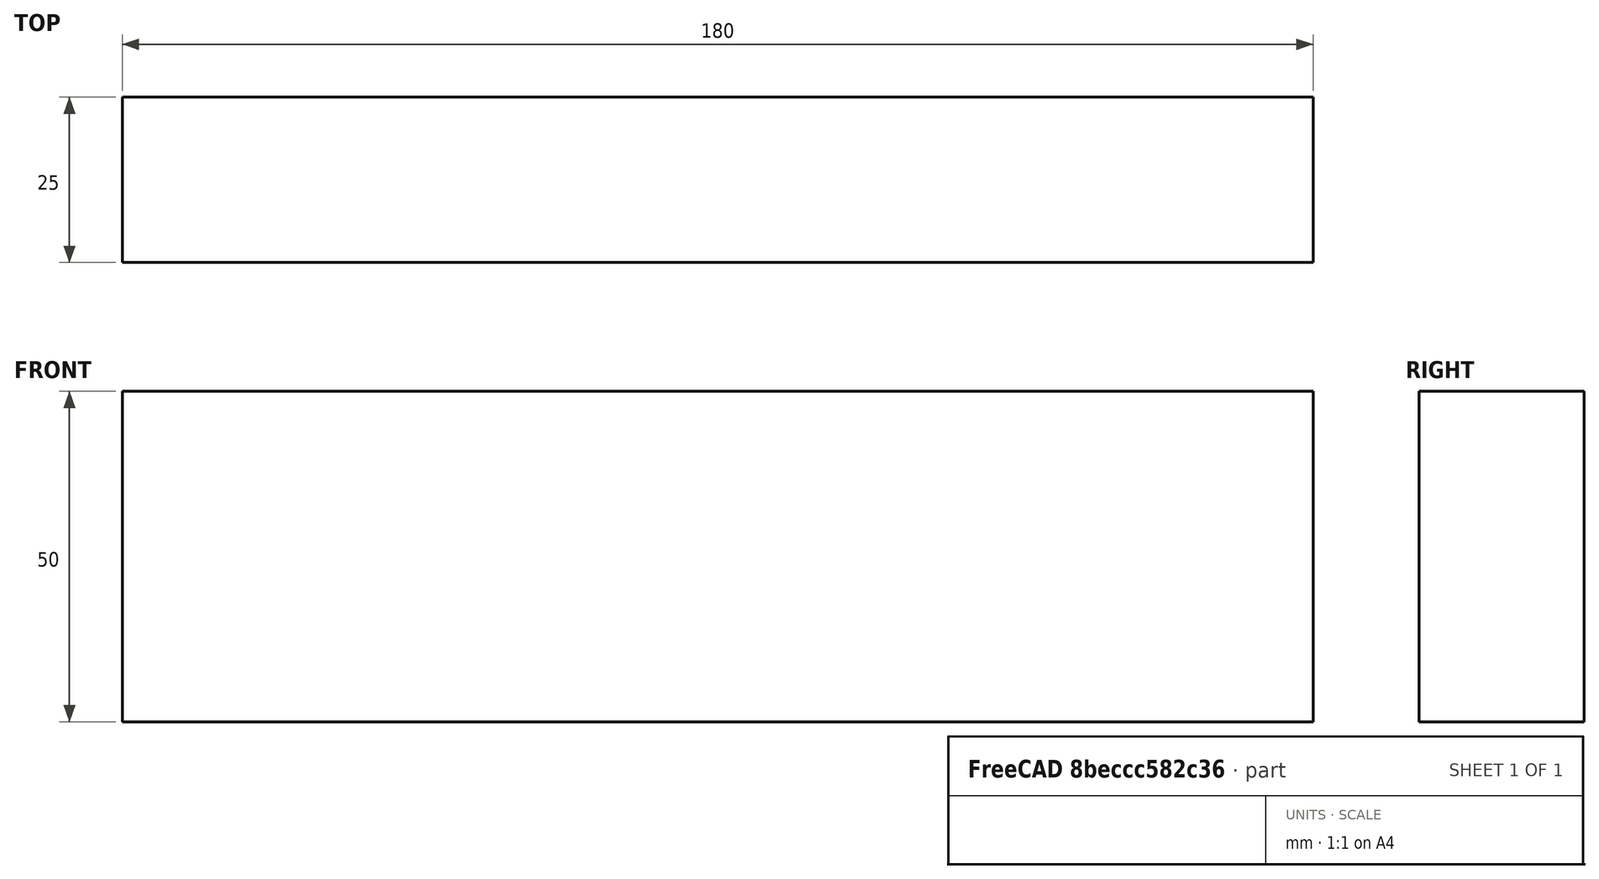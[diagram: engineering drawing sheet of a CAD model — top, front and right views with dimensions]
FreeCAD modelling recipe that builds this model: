
FCSTD DOCUMENT  (FreeCAD 0.15R4671 (Git))
Label: Flat Bar 180x25 EN10058 S235JR
License: All rights reserved
LicenseURL: http://en.wikipedia.org/wiki/All_rights_reserved
objects: Sketcher::SketchObject×1, Part::Extrusion×1
note: 2 computed .brp shape members not serialized (recipe doc carries the construction recipe); baked Part::Feature solids carry a one-line shape summary decoded from their .brp

FEATURE [Sketcher::SketchObject] Sketch
  sketch-geometry (4):
    g0: LineSegment StartX=-90 StartY=-12.5 StartZ=0 EndX=90 EndY=-12.5 EndZ=0
    g1: LineSegment StartX=90 StartY=-12.5 StartZ=0 EndX=90 EndY=12.5 EndZ=0
    g2: LineSegment StartX=90 StartY=12.5 StartZ=0 EndX=-90 EndY=12.5 EndZ=0
    g3: LineSegment StartX=-90 StartY=12.5 StartZ=0 EndX=-90 EndY=-12.5 EndZ=0
  constraints (12):
    c: Coincident(g0,g1)
    c: Coincident(g1,g2)
    c: Coincident(g2,g3)
    c: Coincident(g3,g0)
    c: Horizontal(g0)
    c: Horizontal(g2)
    c: Vertical(g1)
    c: Vertical(g3)
    c: Symmetric(g1,g2,g-2)
    c: Symmetric(g0,g1,g-1)
    c: DistanceY(g1) = 25
    c: DistanceX(g0) = 180
FEATURE [Part::Extrusion] Extrude  label="Flat Bar 180x25 EN10058 S235JR"
  Base = -> Sketch
  Dir = (0,0,50)
  Solid = true
